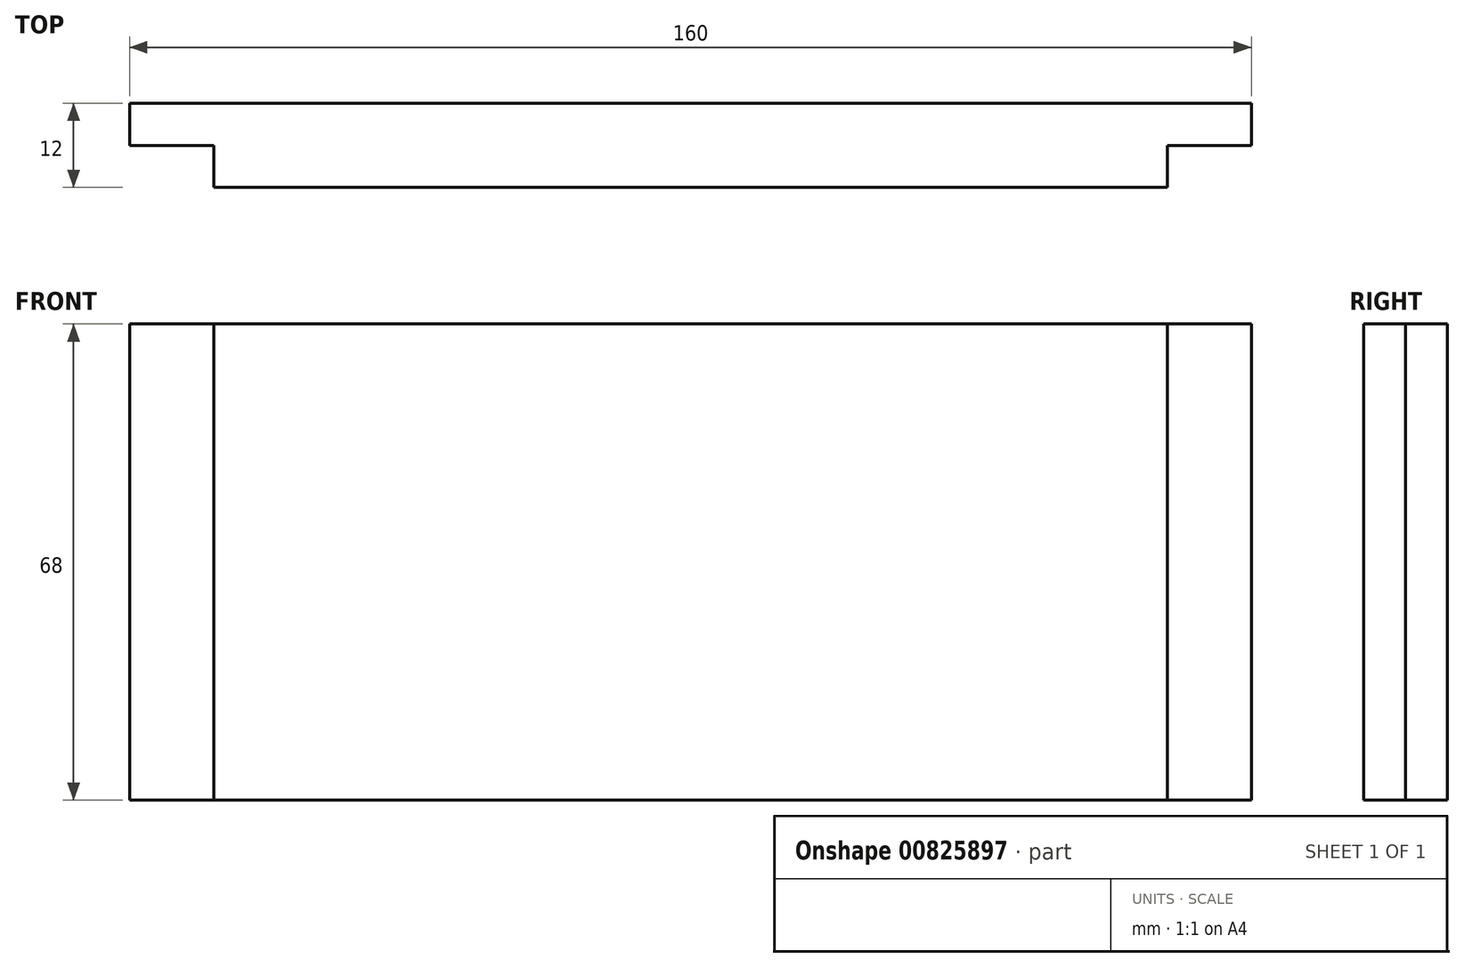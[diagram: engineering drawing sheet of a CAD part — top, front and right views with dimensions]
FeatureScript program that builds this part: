
annotation { "Feature Type Name" : "Feature", "Feature Type Description" : "" }
export const myFeature = defineFeature(function(context is Context, id is Id, definition is map)
    precondition{}
    {
        {
            var Q0;
            Q0=qCreatedBy(makeId("Front.planeOp"),FACE);
            var sketch = newSketch(context, id + "F0", { "sketchPlane" : qUnion([Q0])});
            skLineSegment(sketch, "E0.bottom", {"start": v(80, 34) * mm, "end": v(-80, 34) * mm});
            skLineSegment(sketch, "E0.top", {"start": v(80, -34) * mm, "end": v(-80, -34) * mm});
            skLineSegment(sketch, "E0.left", {"start": v(80, 34) * mm, "end": v(80, -34) * mm});
            skLineSegment(sketch, "E0.right", {"start": v(-80, 34) * mm, "end": v(-80, -34) * mm});
            skPoint(sketch, "E0.middle", {"position": v(0, 0) * mm});
            skSolve(sketch);
        }
        {
            var Q0;
            Q0 = qSketchRegion(id + "F0", true);
            extrude(context, id + "F1", {"entities" : qUnion([Q0]), "depth" : 12 * mm, "offsetDistance" : 25 * mm});
        }
        {
            var Q0;
            Q0=makeQuery(id+"F1.opExtrude","SWEPT_FACE",FACE,{"disambiguationData":[OSD([sQuery(id+"F0.wireOp",EDGE,"E0.left")])]});
            var sketch = newSketch(context, id + "F2", { "sketchPlane" : qUnion([Q0])});
            skLineSegment(sketch, "E1", {"start": v(-6, 34) * mm, "end": v(-6, 22) * mm});
            skLineSegment(sketch, "E2", {"start": v(-6, 22) * mm, "end": v(-6, -34) * mm});
            skSolve(sketch);
        }
        {
            var Q0;
            {var subQ0=sQuery(id+"F2.wireOp",EDGE,"E1");Q0=makeQuery(id+"F2.imprint","IMPRINT",FACE,{"disambiguationData":[TD([[makeQuery(id+"F2.imprint","IMPRINT",EDGE,{"derivedFrom":subQ0}),-1.0]])]});}
            extrude(context, id + "F3", {"entities" : qUnion([Q0]), "operationType" : NewBodyOperationType.REMOVE, "oppositeDirection" : true, "depth" : 12 * mm, "offsetDistance" : 25 * mm});
        }
        {
            var Q0;
            Q0=makeQuery(id+"F1.opExtrude","SWEPT_FACE",FACE,{"disambiguationData":[OSD([sQuery(id+"F0.wireOp",EDGE,"E0.right")])]});
            var sketch = newSketch(context, id + "F4", { "sketchPlane" : qUnion([Q0])});
            skLineSegment(sketch, "E3", {"start": v(6, 34) * mm, "end": v(6, -34) * mm});
            skSolve(sketch);
        }
        {
            var Q0;
            {var subQ0=sQuery(id+"F4.wireOp",EDGE,"E3");Q0=makeQuery(id+"F4.imprint","IMPRINT",FACE,{"disambiguationData":[TD([[makeQuery(id+"F4.imprint","IMPRINT",EDGE,{"derivedFrom":subQ0}),1.0]])]});}
            extrude(context, id + "F5", {"entities" : qUnion([Q0]), "operationType" : NewBodyOperationType.REMOVE, "oppositeDirection" : true, "depth" : 12 * mm, "offsetDistance" : 25 * mm});
        }
    });
